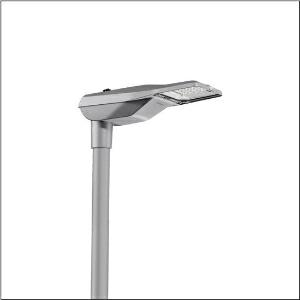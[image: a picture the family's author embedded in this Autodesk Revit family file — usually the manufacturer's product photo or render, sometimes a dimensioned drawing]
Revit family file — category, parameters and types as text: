
# Revit family: streetlight_sl_21_iq_micro___st1_0ab_5xe1m31v08db_4fb3
name_source: partatom
category: Lighting Fixtures
units: mm (PartAtom-declared; Revit-internal decimal feet)

## family parameters
Cut with Voids When Loaded = No
Host = Face
Light Source = No
Part Type = Normal
Room Calculation Point = No
Round Connector Dimension = Use Diameter
Shared = No

## types (1)
- --- (1 x LED, 4490 lm, 39.1 W, 3000K)
    Apparent Load = 39 VA
    CIE Flux Codes = 38 73 97 100 100
    Color Rendering = 70
    Color Temperature = 3000K
    Default Elevation = 1800 mm
    Description = Streetlight SL 21 iQ micro, mast luminaire, primary light control with lens, of PMMA, primary optical cover: cover, of toughened safety glass, transparent, light distribution: ST1.0aB, light emission: direct distribution, primary light characteristic: asymmetric, installation type: post-top, side-entry, LED, High Power LED, rated luminous flux: 4.490lm, luminous efficacy: 115lm/W, light colour: 730, colour temperature: 3000K, control: presetting dimming logarithmic, Street-Remote, Auto-Match, Temp-Guard, Lumen-Switch, Night-Set, Smart-Wire, Light-Fading, Desk-Remote (wireless, voltage-free reading and setting of iQ features in the workshop via application-optimized NFC function/RFID function), optimised constant luminous flux control (CLO 2.0), mains connection: 220..240V, AC, 50/60Hz, start of lifetime: 39W, end of service life: 41W, reduction: 17W, luminaire housing, of diecast aluminium, powder-coated, Siteco® metallic grey (DB 702S), corrosivity category C5 mid according to DIN EN ISO 12944, please order mast flange separately, inclination adjustable: 0°, 5°, 10°, 15°, sealing non-destructively replaceable, multi-level sealing system, length: 528mm, width: 235mm, height: 110mm, mast flange for spigot size: 42mm (side-entry): 5XC10008XM4, 60/48mm (side-entry/post-top): 5XC10108XM2, 76/60mm (side-entry/post-top): 5XC10108XM1, Smart Interface above, protection rating (complete): IP66, insulation class (complete): insulation class II (safety insulation), certification: CE, ENEC, ENEC+, VDE, impact resistance: IK09, permissible operating ambient temperature for outdoor applications: -40..+50°C, standard-compliant lighting for roads and squares, packaging unit: 1 piece

Light Distribution: ST1.0aB
    Height = 110 mm
    Lamp = 1 x LED
    Lamp Light Flux = 4490 lm
    Lamp Power = 39.1 W
    Lamp count = 1
    Length = 528 mm
    Luminous efficacy = 115 lm/W
    Manufacturer = Siteco
    ModVariant = No
    Model = 5XE1M31V08DB
    Number of Poles = 1
    OnlyDefault = Yes
    Power Factor = 1
    Product Name = Streetlight SL 21 iQ micro | ST1.0aB
    Product group = mast luminaire | pylon top
    ProductGroupID = 6100
    Protection Class = Protection class II
    Protection Degree = IP 66
    RLX_Detail_Level = 1
    RLX_Emergency_Light_Flux = 0 lm
    RLX_Emergency_Type = 0
    RLX_Emergency_Type_DB = No
    RlxData = <blob elided: 98145 chars, md5=42ab1e68>
    Socket = socket
    Standby Power = 0 W
    System Light Flux = 4490 lm
    System Power = 39 W
    Type Comments = factory setting: luminous flux: 100 % | dim-lin: 254 | 765 mA
    Type Image = l_1277292.jpg
    URL = http://relux.com
    VarID = @adj_042793
    Voltage = 0 V
    Weight = 0.00 kg
    Width = 235 mm

## geometry (parser evidence)
native form markers: Blend x4, Sweep x11
no freeform markers — native parametric forms only
